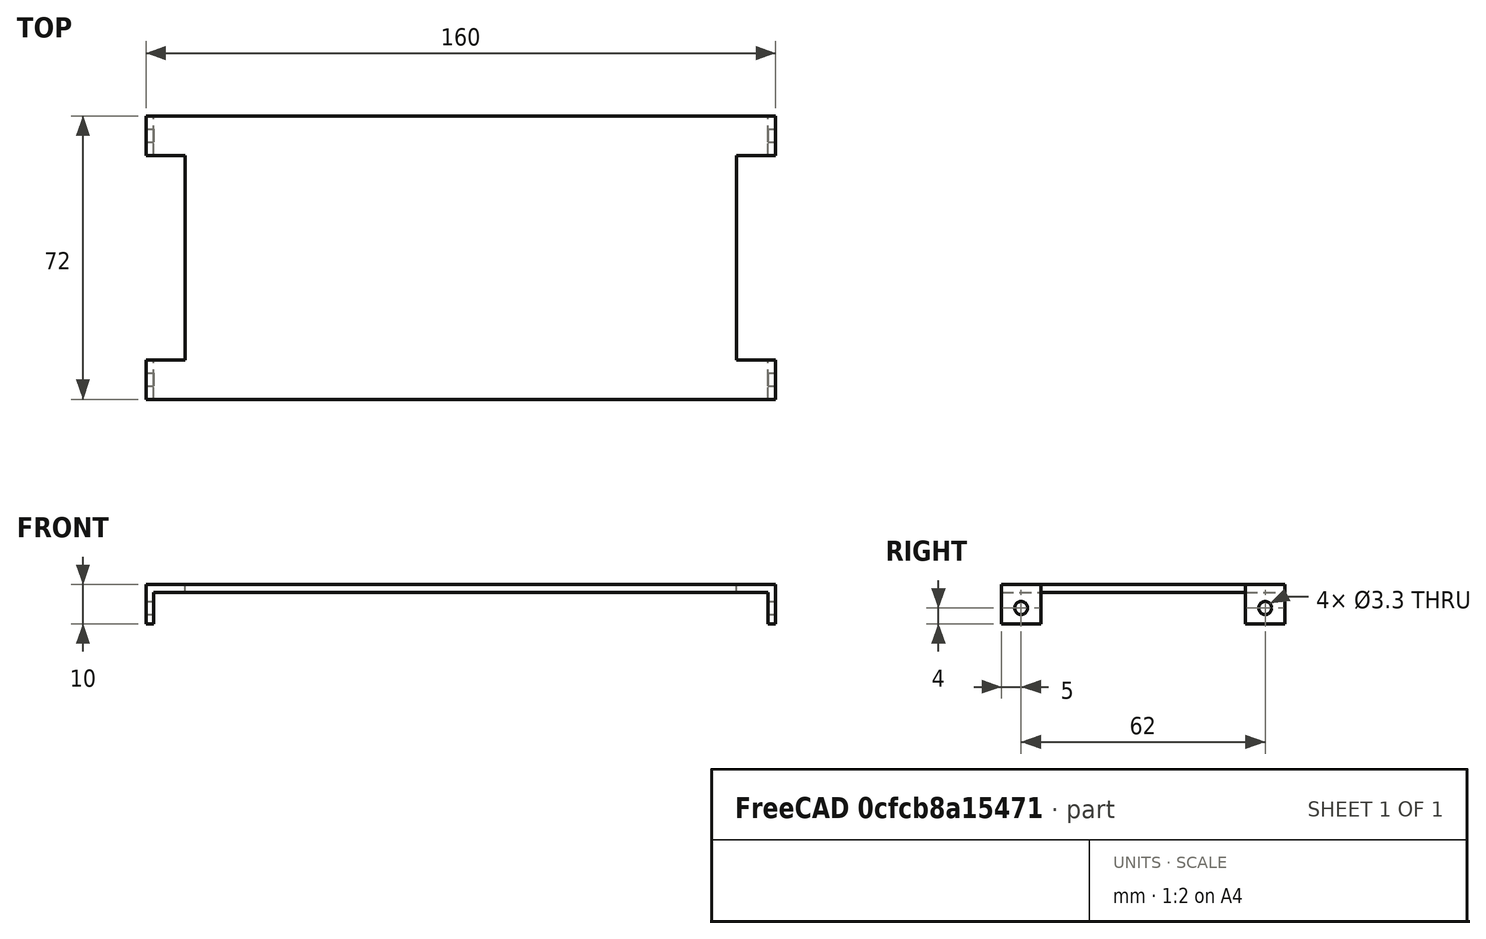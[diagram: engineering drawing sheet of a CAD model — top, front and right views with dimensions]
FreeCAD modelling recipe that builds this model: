
FCSTD DOCUMENT  (FreeCAD 0.17R13522 (Git))
Label: Zwischenblech_akku
License: All rights reserved
LicenseURL: http://en.wikipedia.org/wiki/All_rights_reserved
objects: TechDraw::DrawViewDimension×12, Part::Box×3, Part::Cut×3, TechDraw::DrawProjGroupItem×3, Sketcher::SketchObject×2, Part::Mirroring×1, PartDesign::FeatureBase×1, PartDesign::Hole×1, TechDraw::DrawSVGTemplate×1, PartDesign::Body×1, TechDraw::DrawProjGroup×1, TechDraw::DrawPage×1
note: 13 computed .brp shape members not serialized (recipe doc carries the construction recipe); baked Part::Feature solids carry a one-line shape summary decoded from their .brp

FEATURE [Part::Box] Box  label="Würfel"
  AttacherType = Attacher::AttachEngine3D
  Height = 10
  Length = 160
  Width = 72
FEATURE [Part::Box] Box001  label="Würfel001"
  AttacherType = Attacher::AttachEngine3D
  Height = 10
  Length = 10
  Placement = pos=(0,10,0) rot=(0,0,1;0rad)
  Width = 52
FEATURE [Part::Mirroring] Part__Mirroring  label="Würfel001 (Mirror #1)"
  Base = (80,0,0)
  Normal = (1,0,0)
  Source = -> Box001
FEATURE [Part::Cut] Cut
  Base = -> Box
  Tool = -> Box001
FEATURE [Part::Cut] Cut001
  Base = -> Cut
  Tool = -> Part__Mirroring
FEATURE [Part::Box] Box002  label="Würfel002"
  AttacherType = Attacher::AttachEngine3D
  Height = 8
  Length = 156
  Placement = pos=(2,0,0) rot=(0,0,1;0rad)
  Width = 72
FEATURE [Part::Cut] Cut002
  Base = -> Cut001
  Tool = -> Box002
FEATURE [PartDesign::FeatureBase] BaseFeature
  BaseFeature = -> Cut002
FEATURE [Sketcher::SketchObject] Sketch
  MapMode = 5
  Placement = pos=(0,0,0) rot=(0.57735,-0.57735,-0.57735;2.0944rad)
  Support = -> [BaseFeature]
  sketch-geometry (2):
    g0: Circle CenterX=-5 CenterY=4 CenterZ=0 NormalX=0 NormalY=0 NormalZ=1 AngleXU=0 Radius=2.2
    g1: Circle CenterX=-67 CenterY=4 CenterZ=0 NormalX=0 NormalY=0 NormalZ=1 AngleXU=0 Radius=2.2
  constraints (6):
    c: Horizontal(g0,g1)
    c: DistanceY(g-1,g0) = 4
    c: Radius(g0) = 2.2
    c: Radius(g1) = 2.2
    c: DistanceX(g0,g-1) = 5
    c: DistanceX(g1,g-1) = 67
FEATURE [PartDesign::Hole] Hole
  BaseFeature = -> BaseFeature
  Depth = 25
  DepthType = 1
  Diameter = 3.3
  DrillPoint = 1
  DrillPointAngle = 118
  HoleCutCountersinkAngle = 90
  HoleCutDepth = 0
  HoleCutDiameter = 3
  HoleCutType = 0
  ModelActualThread = false
  Profile = -> Sketch
  Tapered = false
  TaperedAngle = 90
  ThreadAngle = 0
  ThreadClass = 0
  ThreadCutOffInner = 0
  ThreadCutOffOuter = 0
  ThreadDirection = 0
  ThreadFit = 0
  ThreadPitch = 0
  ThreadSize = 3
  ThreadType = 1
  Threaded = false
FEATURE [TechDraw::DrawSVGTemplate] Template
  EditableTexts = Designed_by_Name=Christian Dengler; FC-Date=25.04.2018; FC-SC=Scale; FC-SH=1/1; FC-Title=Zwischenblech
  Height = 210
  Orientation = 1
  Width = 297
FEATURE [Sketcher::SketchObject] Sketch001
  MapMode = 5
  Placement = pos=(0,0,10) rot=(0,0,1;0rad)
  Support = -> [Hole]
  sketch-geometry (6):
    g0: Circle CenterX=45 CenterY=58 CenterZ=0 NormalX=0 NormalY=0 NormalZ=1 AngleXU=0 Radius=2
    g1: Circle CenterX=120 CenterY=58 CenterZ=0 NormalX=0 NormalY=0 NormalZ=1 AngleXU=0 Radius=2
    g2: Circle CenterX=130 CenterY=36 CenterZ=0 NormalX=0 NormalY=0 NormalZ=1 AngleXU=0 Radius=2
    g3: Circle CenterX=120 CenterY=8 CenterZ=0 NormalX=0 NormalY=0 NormalZ=1 AngleXU=0 Radius=2
    g4: Circle CenterX=45 CenterY=8 CenterZ=0 NormalX=0 NormalY=0 NormalZ=1 AngleXU=0 Radius=2
    g5: Circle CenterX=20 CenterY=36 CenterZ=0 NormalX=0 NormalY=0 NormalZ=1 AngleXU=0 Radius=2
  constraints (14):
    c: Vertical(g4,g0)
    c: Vertical(g1,g3)
    c: Horizontal(g0,g1)
    c: Horizontal(g4,g3)
    c: Horizontal(g5,g2)
    c: Radius(g5) = 2
    c: Equal(g5, g0-g4) x5
    c: DistanceY(g4,g0) = 50
    c: DistanceX(g4,g3) = 75
    c: DistanceX(g-1,g4) = 45
    c: DistanceY(g-1,g4) = 8
    c: DistanceX(g5,g2) = 110
    c: DistanceY(g-1,g5) = 36
    c: DistanceX(g-1,g5) = 20
FEATURE [PartDesign::Body] Body
  BaseFeature = -> Cut002
  Group = -> [BaseFeature,Sketch,Hole,Sketch001]
  Origin = -> Origin
  Tip = -> Hole
FEATURE [TechDraw::DrawProjGroupItem] ProjItem  label="Front"
  CoarseView = false
  Direction = (0,-1,0)
  Focus = 100
  HardHidden = false
  IsoCount = 0
  IsoHidden = false
  IsoVisible = false
  LockPosition = false
  Perspective = false
  Rotation = 0
  RotationVector = (1,0,0)
  ScaleType = 0
  SeamHidden = false
  SeamVisible = false
  SmoothHidden = false
  SmoothVisible = false
  Source = -> [Body]
  Type = 0
  X = 0
  Y = 63.9337
FEATURE [TechDraw::DrawProjGroupItem] ProjItem001  label="Top"
  CoarseView = false
  Direction = (0,0,1)
  Focus = 100
  HardHidden = false
  IsoCount = 0
  IsoHidden = false
  IsoVisible = false
  LockPosition = false
  Perspective = false
  Rotation = 0
  RotationVector = (1,0,0)
  ScaleType = 0
  SeamHidden = false
  SeamVisible = false
  SmoothHidden = false
  SmoothVisible = false
  Source = -> [Body]
  Type = 4
  X = 0
  Y = -72.6
FEATURE [TechDraw::DrawProjGroupItem] ProjItem002  label="Left"
  CoarseView = false
  Direction = (-1,0,0)
  Focus = 100
  HardHidden = false
  IsoCount = 0
  IsoHidden = false
  IsoVisible = false
  LockPosition = true
  Perspective = false
  Rotation = 0
  RotationVector = (0,1,0)
  ScaleType = 0
  SeamHidden = false
  SeamVisible = false
  SmoothHidden = false
  SmoothVisible = false
  Source = -> [Body]
  Type = 1
  X = 132.721
  Y = 0
FEATURE [TechDraw::DrawProjGroup] ProjGroup
  Anchor = -> ProjItem
  AutoDistribute = true
  CubeDirs = (6) [(1.22465e-16,-2.44929e-16,-1),(1.93086e-32,-1,2.44929e-16),(-1,-2.46519e-32,-1.22465e-16),(-1.93086e-32,1,-2.44929e-16),(1,2.46519e-32,1.22465e-16),(-1.22465e-16,2.44929e-16,1)]
  CubeRotations = (6) [(1,2.46519e-32,1.22465e-16),(1,2.46519e-32,1.22465e-16),(4.89859e-16,1,-3.67394e-16),(-1,-2.46519e-32,-1.22465e-16),(-4.89859e-16,-1,3.67394e-16),(1,2.46519e-32,1.22465e-16)]
  LockPosition = false
  ProjectionType = 0
  Rotation = 0
  Scale = 0.8
  ScaleType = 2
  Source = -> [Body]
  Views = -> [ProjItem,ProjItem001,ProjItem002]
  X = 86.5544
  Y = 185.3
  spacingX = 15
  spacingY = 15
FEATURE [TechDraw::DrawViewDimension] Dimension
  FormatSpec = %.2f
  LockPosition = false
  MeasureType = 1
  References2D = -> [ProjItem002]
  Rotation = 0
  ScaleType = 0
  Type = 1
  X = 10.2351
  Y = -17.5972
FEATURE [TechDraw::DrawViewDimension] Dimension001
  FormatSpec = %.2f
  LockPosition = false
  MeasureType = 1
  References2D = -> [ProjItem002]
  Rotation = 0
  ScaleType = 0
  Type = 1
  X = 0.987597
  Y = -25.0491
FEATURE [TechDraw::DrawViewDimension] Dimension002
  FormatSpec = %.2f
  LockPosition = false
  MeasureType = 1
  References2D = -> [ProjItem002]
  Rotation = 0
  ScaleType = 0
  Type = 2
  X = 47.8334
  Y = -23.0061
FEATURE [TechDraw::DrawViewDimension] Dimension003
  FormatSpec = %.2f
  LockPosition = false
  MeasureType = 1
  References2D = -> [ProjItem002]
  Rotation = 0
  ScaleType = 0
  Type = 2
  X = 56.1444
  Y = -22.5771
FEATURE [TechDraw::DrawViewDimension] Dimension004
  FormatSpec = %.2f
  LockPosition = false
  MeasureType = 1
  References2D = -> [ProjItem001]
  Rotation = 0
  ScaleType = 0
  Type = 2
  X = 71.7869
  Y = -7.74972
FEATURE [TechDraw::DrawViewDimension] Dimension005
  FormatSpec = %.2f
  LockPosition = false
  MeasureType = 1
  References2D = -> [ProjItem001]
  Rotation = 0
  ScaleType = 0
  Type = 2
  X = 82.1879
  Y = -8.36155
FEATURE [TechDraw::DrawViewDimension] Dimension006
  FormatSpec = %.2f
  LockPosition = false
  MeasureType = 1
  References2D = -> [ProjItem001]
  Rotation = 0
  ScaleType = 0
  Type = 2
  X = 93.2006
  Y = -7.54579
FEATURE [TechDraw::DrawViewDimension] Dimension007
  FormatSpec = %.2f
  LockPosition = false
  MeasureType = 1
  References2D = -> [ProjItem001]
  Rotation = 0
  ScaleType = 0
  Type = 1
  X = 37.5902
  Y = 36.7092
FEATURE [TechDraw::DrawViewDimension] Dimension008
  FormatSpec = %.2f
  LockPosition = false
  MeasureType = 1
  References2D = -> [ProjItem001]
  Rotation = 0
  ScaleType = 0
  Type = 1
  X = 37.2966
  Y = 44.0511
FEATURE [TechDraw::DrawViewDimension] Dimension009
  FormatSpec = %.2f
  LockPosition = false
  MeasureType = 1
  References2D = -> [ProjItem001]
  Rotation = 0
  ScaleType = 0
  Type = 1
  X = 8.81021
  Y = 53.4486
FEATURE [TechDraw::DrawViewDimension] Dimension010
  FormatSpec = %.2f
  LockPosition = false
  MeasureType = 1
  References2D = -> [ProjItem]
  Rotation = 0
  ScaleType = 0
  Type = 1
  X = 50.0335
  Y = -8.66212
FEATURE [TechDraw::DrawViewDimension] Dimension011
  FormatSpec = %.2f
  LockPosition = false
  MeasureType = 1
  References2D = -> [ProjItem002]
  Rotation = 0
  ScaleType = 0
  Type = 5
  X = -52.7117
  Y = 9.58519
FEATURE [TechDraw::DrawPage] Page
  KeepUpdated = true
  ProjectionType = 0
  Template = -> Template
  Views = -> [ProjGroup,Dimension,Dimension001,Dimension002,Dimension003,Dimension004,Dimension005,Dimension006,Dimension007,Dimension008,Dimension009,Dimension010,Dimension011]
